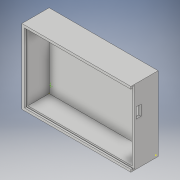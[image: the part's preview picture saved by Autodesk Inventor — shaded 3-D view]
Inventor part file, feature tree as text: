
AUTODESK INVENTOR PART (.ipt)
format: ipt  version: 2018.3 (Build 223284000, 284)  size: 162,304 bytes
history: native  units: in
note: dims shown in document units (in); Inventor stores cm internally (conversion verified against a paired STEP export)
features: sketch x14, extrude x5, other x3, shell x1, split x1, delete_face x1
ambient origin geometry x8: Origin, YZ Plane, XZ Plane, XY Plane, X Axis, Y Axis, Z Axis, Center Point
bodies: Solid1 (feature_tree)
feature tree (25):
  extrude  "Extrusion1"  Depth=2.2047in
  shell  "Shell1"  Thickness=0.7874in
  split  "Split1"
  delete_face  "Delete Face1"
  sketch  "Sketch3"  dims[d6=0.3346in d7=0.7874in d8=0.394in d9=0.0in d10=0.0in]
  sketch  "Sketch4"  dims[d11=0.05in d12=0.04in d13=0.0584in d14=0.05in d15=0.12in d16=0.08in d17=0.009in d18=0.03in d19=0.481in d20=0.3436in]
  other  "Snap Fit1"
  other  "Snap Fit2"
  extrude  "Extrusion2"  Depth=0.1575in
  extrude  "Extrusion3"  Depth=0.7874in TaperAngle=0.0deg
  extrude  "Extrusion4"  Depth=2.3in
  sketch  "Sketch10"  dims[d39=0.11in d40=0.0in]
  sketch  "Sketch11"
  sketch  "Sketch12"
  sketch  "Sketch13"
  sketch  "Sketch14"
  sketch  "Sketch1"  dims[d0=3.3071in d1=2.2047in d2=0.7874in d3=0.0in]
  sketch  "Sketch2"  dims[d4=0.0787in d5=0.1575in]
  other  "Srf1"
  sketch  "Sketch5"  dims[d21=0.05in d22=0.04in d23=0.0584in d24=0.05in d25=0.12in d26=0.08in d27=0.009in d28=0.03in d29=0.481in d30=0.3436in d31=2.3in]
  sketch  "Sketch6"  dims[d32=90.0deg d33=0.06in]
  sketch  "Sketch7"  dims[d34=0.031in]
  sketch  "Sketch8"  dims[d35=3.4375in d36=0.0in]
  sketch  "Sketch9"  dims[d37=0.11in d38=0.0in]
  extrude  "ExtrusionSrf1"  Depth=0.06in
